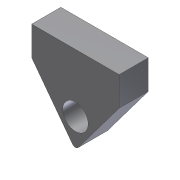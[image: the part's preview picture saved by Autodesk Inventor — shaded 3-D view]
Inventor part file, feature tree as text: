
AUTODESK INVENTOR PART (.ipt)
format: ipt  version: 2012 (Build 160160000, 160)  size: 81,408 bytes
history: native  units: in
note: dims shown in document units (in); Inventor stores cm internally (conversion verified against a paired STEP export)
features: extrude x1, fillet x1, sketch x1
ambient origin geometry x8: Origin, YZ Plane, XZ Plane, XY Plane, X Axis, Y Axis, Z Axis, Center Point
bodies: Solid1 (feature_tree)
feature tree (3):
  extrude  "Extrusion1"  Depth=1.0in
  fillet  "Fillet1"  Radius=2.0in
  sketch  "Sketch1"  dims[d0=3.0in d1=1.0in d2=2.0in d3=0.875in d4=2.0in d5=1.0in d6=0.0in d7=0.125in]
